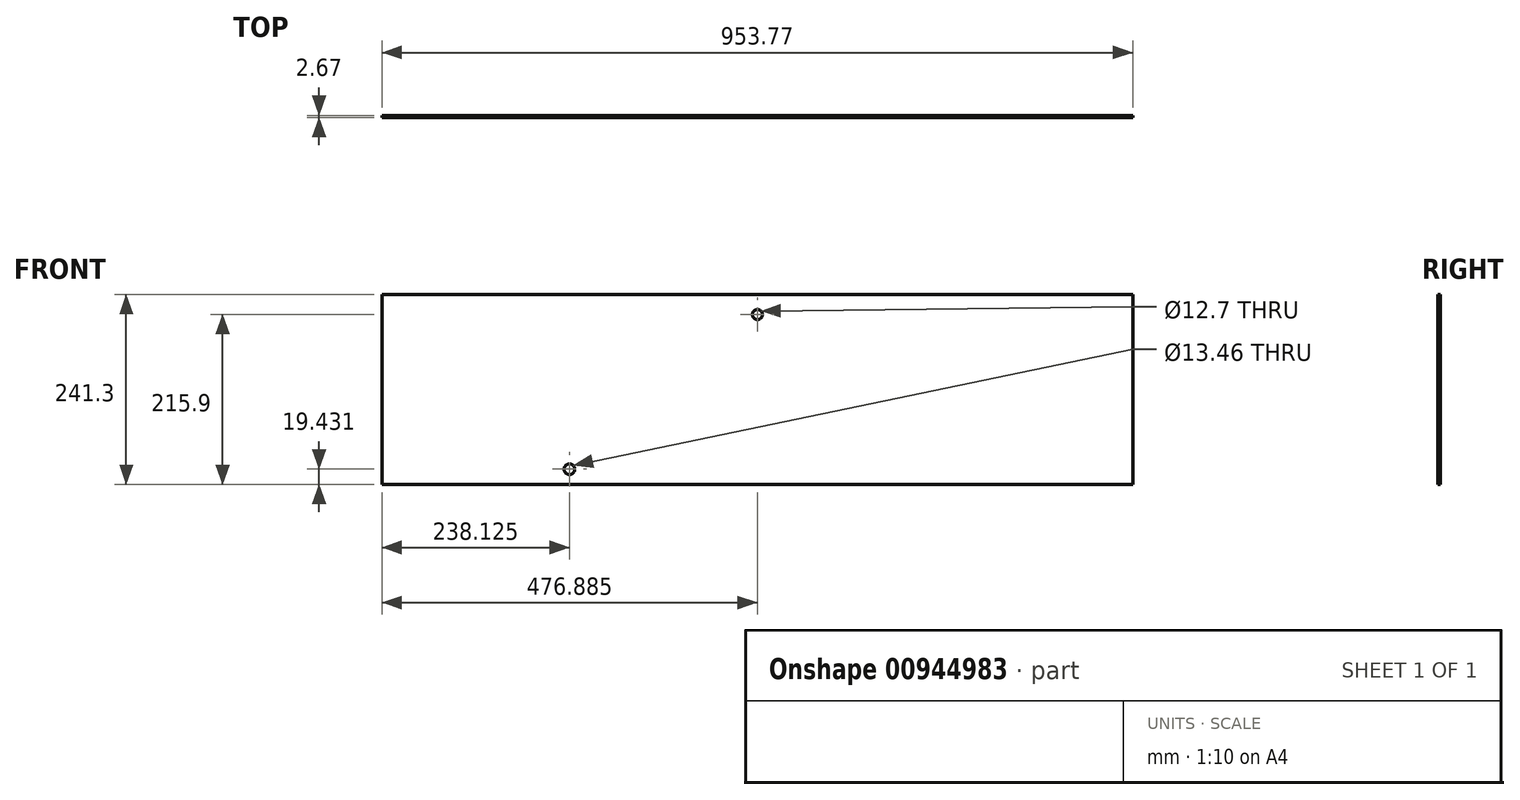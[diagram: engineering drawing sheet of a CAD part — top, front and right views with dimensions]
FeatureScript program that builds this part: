
annotation { "Feature Type Name" : "Feature", "Feature Type Description" : "" }
export const myFeature = defineFeature(function(context is Context, id is Id, definition is map)
    precondition{}
    {
        {
            var Q0;
            Q0=qCreatedBy(makeId("Front.planeOp"),FACE);
            var sketch = newSketch(context, id + "F0", { "sketchPlane" : qUnion([Q0])});
            skLineSegment(sketch, "E0.bottom", {"start": v(0, 0) * mm, "end": v(953.77, 0) * mm});
            skLineSegment(sketch, "E0.top", {"start": v(0, -241.3) * mm, "end": v(953.77, -241.3) * mm});
            skLineSegment(sketch, "E0.left", {"start": v(0, 0) * mm, "end": v(0, -241.3) * mm});
            skLineSegment(sketch, "E0.right", {"start": v(953.77, 0) * mm, "end": v(953.77, -241.3) * mm});
            skCircle(sketch, "E1", {"center": v(476.88, -25.4) * mm, "radius": 6.35 * mm});
            skCircle(sketch, "E2", {"center": v(238.13, -221.87) * mm, "radius": 6.73 * mm});
            skSolve(sketch);
        }
        {
            var Q0;
            Q0 = qSketchRegion(id + "F0", true);
            extrude(context, id + "F1", {"entities" : qUnion([Q0]), "depth" : 2.67 * mm, "offsetDistance" : 25.4 * mm});
        }
    });
